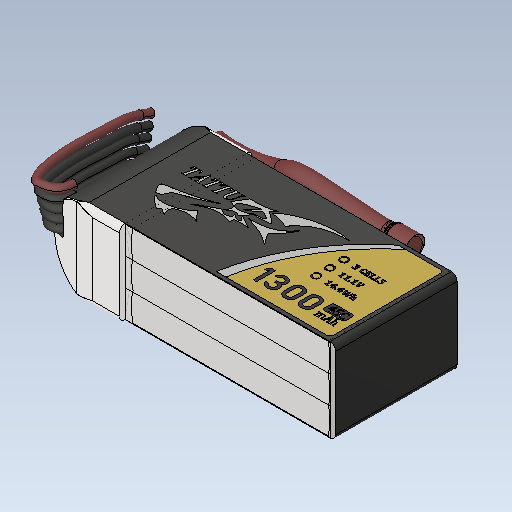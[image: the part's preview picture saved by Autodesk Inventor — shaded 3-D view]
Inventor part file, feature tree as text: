
AUTODESK INVENTOR PART (.ipt)
format: ipt  version: 2020 (Build 240168000, 168)  size: 1,793,536 bytes
history: mixed  units: mm
features: other x18, mirror x2, revolve x2, imported_body x1
ambient origin geometry x8: Origin, YZ Plane, XZ Plane, XY Plane, X Axis, Y Axis, Z Axis, Center Point
bodies: Body1 (imported_parasolid), Body2 (imported_parasolid), Body3 (imported_parasolid), Body4 (imported_parasolid), Body5 (imported_parasolid), Body6 (imported_parasolid), Body7 (imported_parasolid), Body8 (imported_parasolid), Body9 (imported_parasolid), Body10 (imported_parasolid), Body11 (imported_parasolid)
feature tree (23):
  other  "Твердое тело1"
  other  "Твердое тело2"
  other  "Твердое тело3"
  other  "Твердое тело4"
  other  "Твердое тело5"
  other  "Твердое тело6"
  other  "Твердое тело7"
  other  "Твердое тело8"
  other  "Твердое тело9"
  other  "Твердое тело10"
  other  "Твердое тело11"
  other  "Saliente-Extruir2"
  mirror  "Simetría2"
  mirror  "Simetría3"
  other  "Cortar-Extruir8"
  other  "Barrer5[1]"
  other  "Barrer5[2]"
  other  "Barrer5[3]"
  other  "Barrer5[4]"
  other  "Barrer5[5]"
  revolve  "Revolución3"  [1 undecoded]
  revolve  "Revolución4"  [1 undecoded]
  imported_body  NMx_Import_Brep_tag  [imported B-rep: ~21 faces, bbox_mm=None]
note: 2 required parameter values undecoded (feature->parameter linkage not recoverable at this tier; creation-order binding heuristic only, values carry confidence <= 0.55)
